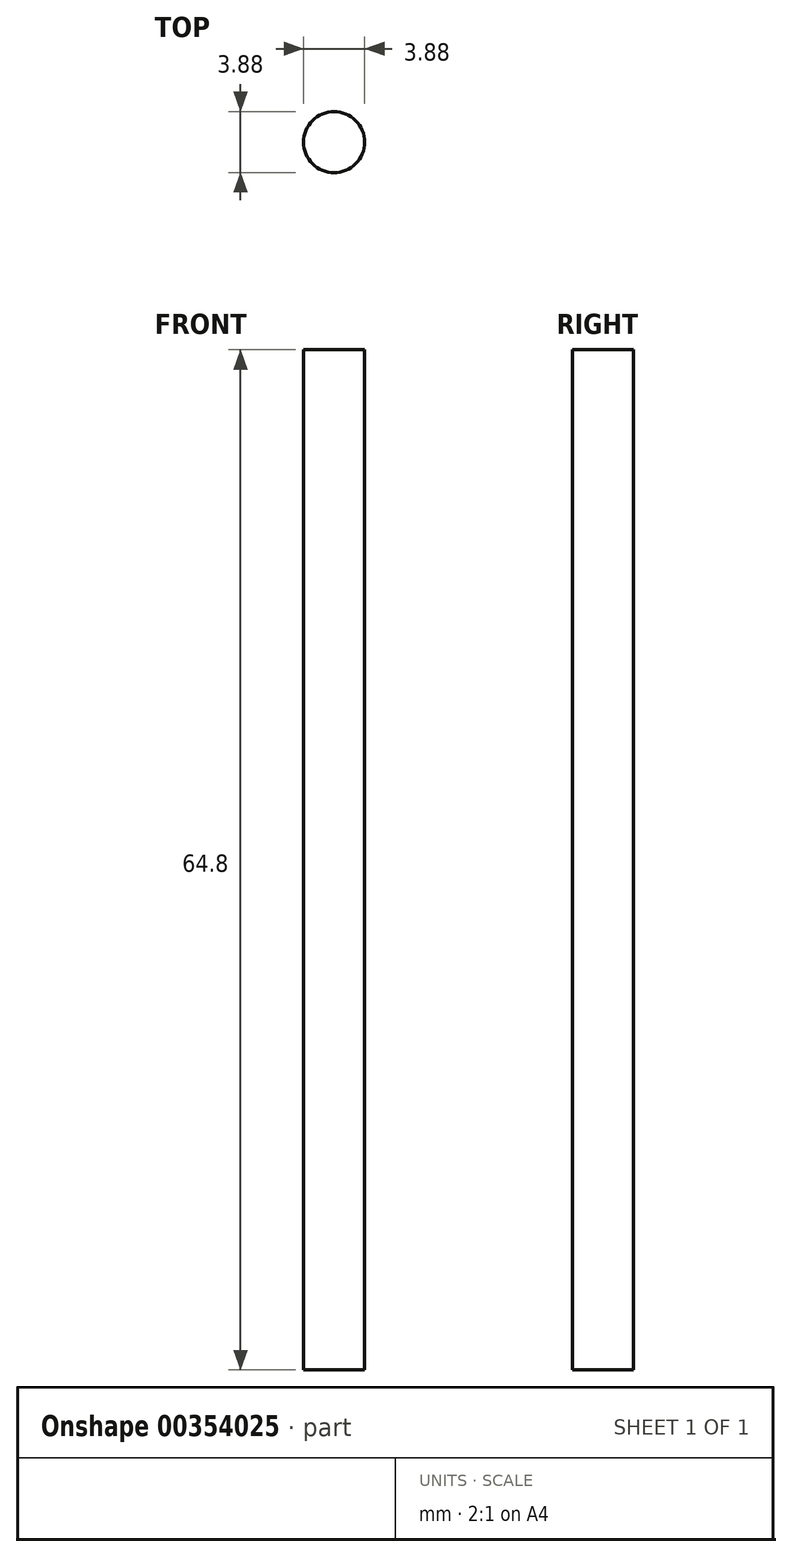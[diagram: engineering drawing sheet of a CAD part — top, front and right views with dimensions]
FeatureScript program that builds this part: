
annotation { "Feature Type Name" : "Feature", "Feature Type Description" : "" }
export const myFeature = defineFeature(function(context is Context, id is Id, definition is map)
    precondition{}
    {
        {
            var Q0;
            Q0=qCreatedBy(makeId("Top.planeOp"),FACE);
            var sketch = newSketch(context, id + "F0", { "sketchPlane" : qUnion([Q0])});
            skCircle(sketch, "E0", {"center": v(0, 0) * mm, "radius": 1.94 * mm});
            skSolve(sketch);
        }
        {
            var Q0;
            Q0 = qSketchRegion(id + "F0", true);
            extrude(context, id + "F1", {"entities" : qUnion([Q0]), "depth" : 64.8 * mm});
        }
    });
